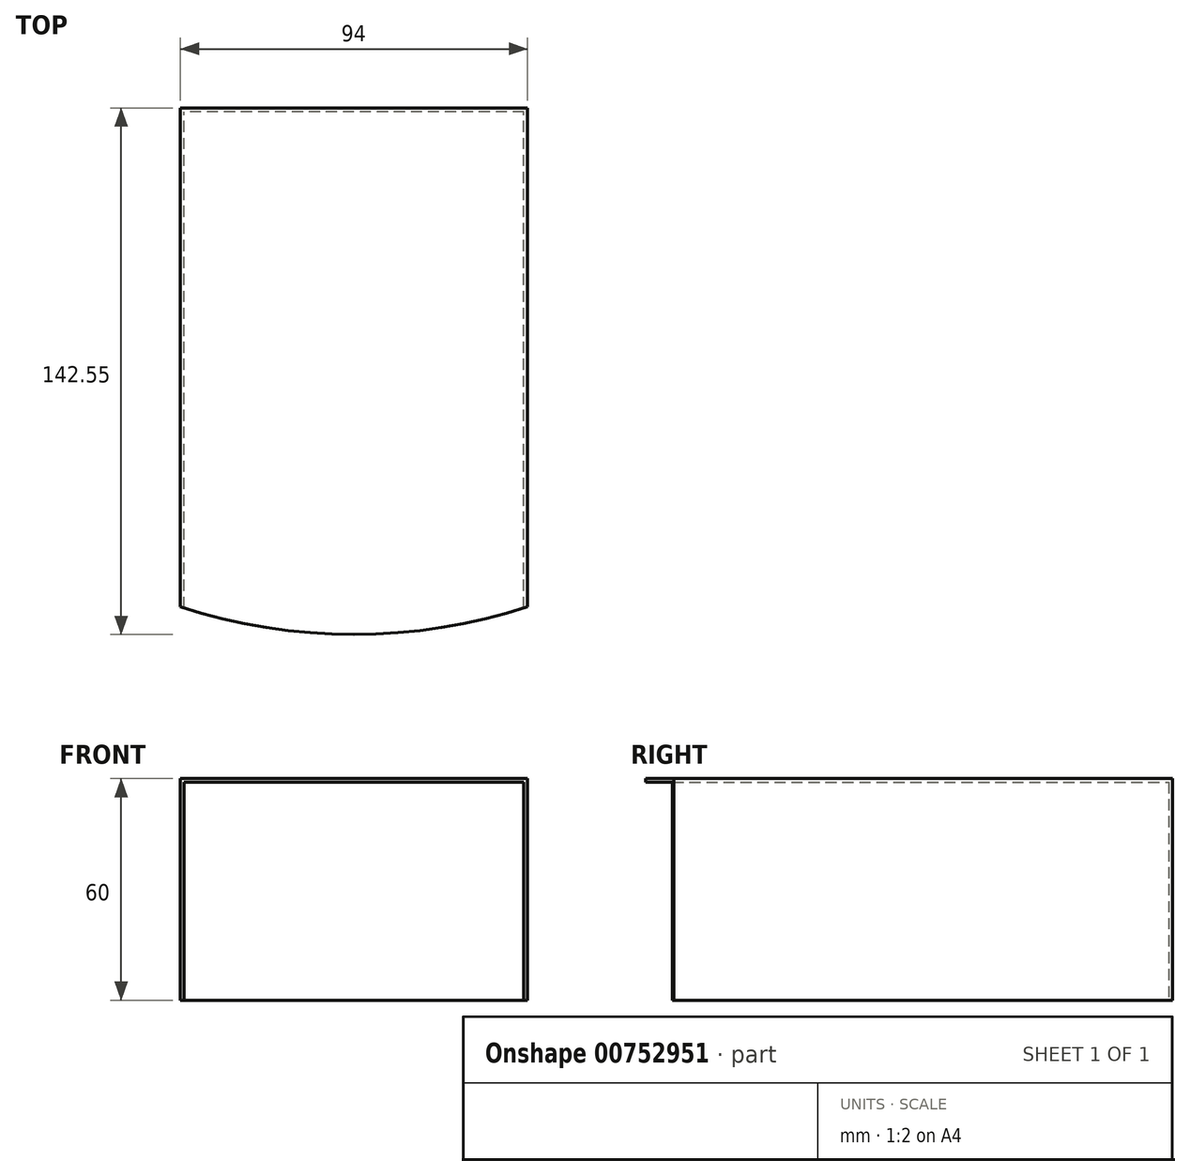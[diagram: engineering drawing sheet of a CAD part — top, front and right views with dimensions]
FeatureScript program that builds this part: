
annotation { "Feature Type Name" : "Feature", "Feature Type Description" : "" }
export const myFeature = defineFeature(function(context is Context, id is Id, definition is map)
    precondition{}
    {
        {
            var Q0;
            Q0=qCreatedBy(makeId("Front.planeOp"),FACE);
            var sketch = newSketch(context, id + "F0", { "sketchPlane" : qUnion([Q0])});
            skLineSegment(sketch, "E0.bottom", {"start": v(47, 30) * mm, "end": v(-47, 30) * mm});
            skLineSegment(sketch, "E0.top", {"start": v(47, -30) * mm, "end": v(-47, -30) * mm});
            skLineSegment(sketch, "E0.left", {"start": v(47, 30) * mm, "end": v(47, -30) * mm});
            skLineSegment(sketch, "E0.right", {"start": v(-47, 30) * mm, "end": v(-47, -30) * mm});
            skPoint(sketch, "E0.middle", {"position": v(0, 0) * mm});
            skSolve(sketch);
        }
        {
            var Q0;
            Q0=makeQuery(id+"F0.imprint","IMPRINT",FACE,{"disambiguationData":[TD([[makeQuery(id+"F0.imprint","IMPRINT",EDGE,{"derivedFrom":sQuery(id+"F0.wireOp",EDGE,"E0.bottom")}),1.0]])]});
            extrude(context, id + "F1", {"entities" : qUnion([Q0]), "depth" : 150 * mm, "offsetDistance" : 25 * mm});
        }
        {
            var Q0;
            Q0=makeQuery(id+"F1.opExtrude","CAP_FACE",FACE,{"disambiguationData":[OSD([sQuery(id+"F0.wireOp",EDGE,"E0.bottom"),sQuery(id+"F0.wireOp",EDGE,"E0.top"),sQuery(id+"F0.wireOp",EDGE,"E0.left"),sQuery(id+"F0.wireOp",EDGE,"E0.right")])],"isStart":false});
            var Q1;
            Q1=makeQuery(id+"F1.opExtrude","SWEPT_FACE",FACE,{"disambiguationData":[OSD([sQuery(id+"F0.wireOp",EDGE,"E0.top")])]});
            shell(context, id + "F2", {"entities" : qUnion([Q0, Q1]), "thickness" : 1 * mm});
        }
        {
            var Q0;
            Q0=makeQuery(id+"F1.opExtrude","SWEPT_FACE",FACE,{"disambiguationData":[OSD([sQuery(id+"F0.wireOp",EDGE,"E0.bottom")])]});
            var sketch = newSketch(context, id + "F3", { "sketchPlane" : qUnion([Q0])});
            skLineSegment(sketch, "E1.0", {"start": v(47, 0) * mm, "end": v(-47, 0) * mm});
            skLineSegment(sketch, "E2.0.1", {"start": v(-47, 0) * mm, "end": v(-47, -150) * mm});
            skLineSegment(sketch, "E2.0.2", {"start": v(-47, -150) * mm, "end": v(47, -150) * mm});
            skLineSegment(sketch, "E2.0.3", {"start": v(47, -150) * mm, "end": v(47, 0) * mm});
            skArc(sketch, "E3", {"start": v(-47, -135) * mm, "mid": v(0, -142.55) * mm, "end": v(47, -135) * mm});
            skSolve(sketch);
        }
        {
            var Q0;
            {var subQ0=sQuery(id+"F3.wireOp",EDGE,"E2.0.2");Q0=makeQuery(id+"F3.imprint","IMPRINT",FACE,{"disambiguationData":[TD([[makeQuery(id+"F3.imprint","IMPRINT",EDGE,{"derivedFrom":subQ0}),-1.0]])]});}
            extrude(context, id + "F4", {"entities" : qUnion([Q0]), "operationType" : NewBodyOperationType.REMOVE, "endBound" : BoundingType.THROUGH_ALL, "oppositeDirection" : true, "depth" : 25 * mm, "offsetDistance" : 25 * mm});
        }
    });
